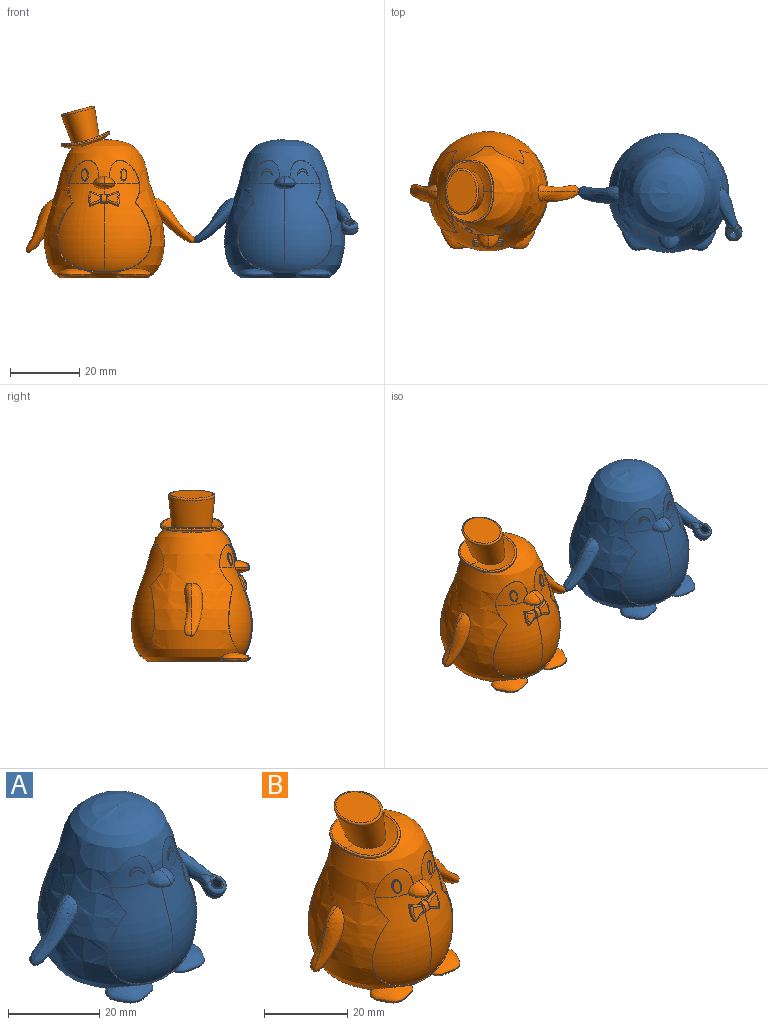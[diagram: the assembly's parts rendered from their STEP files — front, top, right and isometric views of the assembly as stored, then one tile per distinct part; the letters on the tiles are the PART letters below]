
ASSEMBLY  parts=2 mates=1
PART A: 47 faces, bbox 47.7x34.8x41.4 mm
  f0: bspline ~14.59x10.37mm, area 63.4mm2, adj f1,f6,f37,f38,f39,f40,f41
  f1: bspline ~16.09x8.88mm, area 34.3mm2, adj f0,f6,f42
  f2: extruded ~3.22x1.83mm, area 1.6mm2, adj f4,f9,f43,f44
  f3: extruded ~3.04x1.72mm, area 1.2mm2, adj f4,f9,f43,f44
  f4: revolved ~3.35x1.88mm, area 2.4mm2, adj f2,f3,f43,f44
  f5: bspline ~0.66x0.4mm, area 0mm2, adj f6,f15,f28
  f6: revolved ~40x34.78mm, area -613.6mm2, adj f0,f1,f5,f10,f11,f12,f13,f14
  f7: revolved ~25.41x13.46mm, area 325.8mm2, adj f8,f14,f15,f17,f29
  f8: revolved ~25.41x13.46mm, area 325.8mm2, adj f7,f9,f12,f13,f30
  f9: revolved ~8.83x6.78mm, area 49.1mm2, adj f2,f3,f8,f12,f27,f43,f44
  f10: revolved ~32.45x27.32mm, area 791.3mm2, adj f6
  f11: plane 27.91x25mm, normal (0,0,-1), area 565.7mm2, adj f6,f22,f24
  f12: bspline ~12.26x8.93mm, area 5.9mm2, adj f6,f8,f9,f13,f16,f27
  f13: bspline ~20.28x13.66mm, area 7.8mm2, adj f6,f8,f12,f14
  f14: bspline ~20.28x13.66mm, area 7.8mm2, adj f6,f7,f13,f15
  f15: bspline ~12.25x8.92mm, area 5.9mm2, adj f5,f6,f7,f14,f17,f28
  f16: bspline ~0.66x0.4mm, area 0mm2, adj f6,f12,f27
  f17: revolved ~8.83x6.78mm, area 49mm2, adj f7,f15,f18,f19,f28,f45,f46
  f18: extruded ~3.22x1.83mm, area 1.6mm2, adj f17,f20,f45,f46
  f19: extruded ~3.04x1.72mm, area 1.2mm2, adj f17,f20,f45,f46
  f20: revolved ~3.35x1.88mm, area 2.4mm2, adj f18,f19,f45,f46
  f21: bspline ~10.19x8.58mm, area 33.1mm2, adj f6,f22
  f22: bspline ~10.19x8.58mm, area 20.6mm2, adj f6,f11,f21
  f23: bspline ~10.19x8.58mm, area 33.1mm2, adj f6,f24
  f24: bspline ~10.19x8.58mm, area 20.6mm2, adj f6,f11,f23
  f25: bspline ~13.75x13.07mm, area 24.4mm2, adj f6,f26
  f26: bspline ~12.41x11.83mm, area 16mm2, adj f6,f25
  f27: bspline ~4.05x3.2mm, area 14.3mm2, adj f6,f9,f12,f16,f28,f30
  f28: bspline ~4.05x3.2mm, area 14.3mm2, adj f5,f6,f15,f17,f27,f29
  f29: bspline ~3.87x3.19mm, area 6.5mm2, adj f7,f28,f30
  f30: bspline ~3.87x3.19mm, area 6.5mm2, adj f8,f27,f29
  f31: cylinder r=2.43mm len=4.86mm, axis (0,0.5,-0.87), area 10.4mm2, adj f35,f36,f40,f41
  f32: plane 2.9x2.34mm, normal (0,-0.5,0.87), area 1.9mm2, adj f34,f36,f37
  f33: plane 2.87x2.48mm, normal (0,0.5,-0.87), area 2.3mm2, adj f34,f35
  f34: cylinder r=1.15mm len=3.75mm, axis (0,-0.5,0.87), area 21.7mm2, adj f32,f33,f37
  f35: bspline ~4.86x4.39mm, area 16.4mm2, adj f31,f33,f42
  f36: bspline ~4.85x4.09mm, area 15.5mm2, adj f31,f32,f38,f39
  f37: bspline ~1.5x0.98mm, area 1mm2, adj f0,f32,f34,f38,f39
  f38: bspline ~2.14x1.54mm, area 2.6mm2, adj f0,f36,f37,f40
  f39: bspline ~2.69x2.17mm, area 5.3mm2, adj f0,f36,f37,f41
  f40: bspline ~1.14x1.01mm, area 0.9mm2, adj f0,f31,f38,f42
  f41: bspline ~2.7x1.87mm, area 2.2mm2, adj f0,f31,f39,f42
  f42: bspline ~4.24x2.32mm, area 5.8mm2, adj f1,f35,f40,f41
  f43: cylinder r=0.05mm len=0.37mm, axis (0,1,0), area 0mm2, adj f2,f3,f4,f9
  f44: cylinder r=0.05mm len=0.32mm, axis (0,1,0), area 0mm2, adj f2,f3,f4,f9
  f45: cylinder r=0.05mm len=0.32mm, axis (0,1,0), area 0mm2, adj f17,f18,f19,f20
  f46: cylinder r=0.05mm len=0.37mm, axis (0,1,0), area 0mm2, adj f17,f18,f19,f20
PART B: 75 faces, bbox 50.8x36.4x52.7 mm
  f0: bspline ~0.66x0.4mm, area 0mm2, adj f1,f52,f53
  f1: bspline ~12.26x8.93mm, area 5.9mm2, adj f0,f2,f6,f51,f52,f53
  f2: revolved ~8.83x6.78mm, area 45.1mm2, adj f1,f3,f5,f6,f52
  f3: bspline ~3.49x2mm, area 2.9mm2, adj f2,f4,f5
  f4: revolved ~3.11x1.97mm, area 4.5mm2, adj f3
  f5: extruded ~3.5x1.98mm, area 2.3mm2, adj f2,f3
  f6: revolved ~25.41x13.46mm, area 323.8mm2, adj f1,f2,f7,f17,f30,f31,f32,f33
  f7: bspline ~3.87x3.19mm, area 6.5mm2, adj f6,f8,f52
  f8: bspline ~3.87x3.19mm, area 6.5mm2, adj f7,f9,f50
  f9: bspline ~4.05x3.2mm, area 14.3mm2, adj f8,f10,f14,f16,f52,f53
  f10: revolved ~8.83x6.78mm, area 45mm2, adj f9,f11,f13,f14,f50
  f11: bspline ~3.49x2mm, area 2.9mm2, adj f10,f12,f13
  f12: revolved ~3.11x1.97mm, area 4.5mm2, adj f11
  f13: extruded ~3.5x1.98mm, area 2.3mm2, adj f10,f11
  f14: bspline ~12.25x8.92mm, area 5.9mm2, adj f9,f10,f15,f16,f50,f53
  f15: bspline ~20.28x13.66mm, area 7.8mm2, adj f14,f50,f51,f53
  f16: bspline ~0.66x0.4mm, area 0mm2, adj f9,f14,f53
  f17: plane 0.95x0.69mm, normal (1,0,0), area 0.1mm2, adj f6,f18,f29,f32
  f18: plane 2.97x1.31mm, normal (-0.38,-0.32,-0.87), area 1.6mm2, adj f17,f19,f29,f30
  f19: bspline ~0.49x0.24mm, area 0.1mm2, adj f18,f20,f28,f30
  f20: cylinder r=6mm len=4.22mm, axis (0,0.94,-0.34), area 2.2mm2, adj f19,f21,f27,f30
  f21: bspline ~0.49x0.24mm, area 0.1mm2, adj f20,f22,f26,f30
  f22: plane 2.97x1.31mm, normal (-0.38,0.32,0.87), area 1.6mm2, adj f21,f23,f30,f31
  f23: bspline ~3.77x1.71mm, area 2.5mm2, adj f22,f24,f26,f32
  f24: plane 3x2.99mm, normal (0,-0.94,0.34), area 6.2mm2, adj f23,f25,f27,f29
  f25: plane 1.42x0.5mm, normal (1,0,0), area 0.1mm2, adj f24,f29,f32
  f26: bspline ~0.69x0.5mm, area 0.1mm2, adj f21,f23,f27
  f27: bspline ~4.14x1.89mm, area 3.1mm2, adj f20,f24,f26,f28
  f28: bspline ~0.77x0.36mm, area 0.1mm2, adj f19,f27,f29
  f29: bspline ~3.77x1.98mm, area 2.5mm2, adj f17,f18,f24,f25,f28
  f30: plane 4.21x3.51mm, normal (0,0.94,-0.34), area 11.3mm2, adj f6,f18,f19,f20,f21,f22
  f31: plane 0.54x0.21mm, normal (1,0,0), area 0mm2, adj f6,f22,f32
  f32: bspline ~2.79x2.15mm, area 2mm2, adj f6,f17,f23,f25,f31,f33
  f33: extruded ~2.71x1.93mm, area 6.3mm2, adj f6,f32,f34,f50
  f34: bspline ~2.79x2.15mm, area 2mm2, adj f33,f35,f47,f48,f49,f50
  f35: plane 0.95x0.69mm, normal (-1,0,0), area 0.1mm2, adj f34,f36,f46,f50
  f36: plane 2.97x1.31mm, normal (0.38,-0.32,-0.87), area 1.6mm2, adj f35,f37,f45,f46
  f37: plane 4.21x3.51mm, normal (0,0.94,-0.34), area 11.3mm2, adj f36,f38,f39,f44,f45,f50
  f38: plane 2.97x1.31mm, normal (0.38,0.32,0.87), area 1.6mm2, adj f37,f39,f48,f49
  f39: bspline ~0.54x0.26mm, area 0.1mm2, adj f37,f38,f40,f44
  f40: bspline ~0.69x0.5mm, area 0.1mm2, adj f39,f41,f48
  f41: bspline ~4.14x1.89mm, area 3.1mm2, adj f40,f42,f43,f44
  f42: plane 3x2.99mm, normal (0,-0.94,0.34), area 6.2mm2, adj f41,f46,f47,f48
  f43: bspline ~0.77x0.36mm, area 0.1mm2, adj f41,f45,f46
  f44: cylinder r=6mm len=4.22mm, axis (0,0.94,-0.34), area 2.2mm2, adj f37,f39,f41,f45
  f45: bspline ~0.54x0.26mm, area 0.1mm2, adj f36,f37,f43,f44
  f46: bspline ~3.77x1.98mm, area 2.5mm2, adj f35,f36,f42,f43,f47
  f47: plane 1.42x0.5mm, normal (-1,0,0), area 0.1mm2, adj f34,f42,f46
  f48: bspline ~3.77x1.71mm, area 2.5mm2, adj f34,f38,f40,f42
  f49: plane 0.54x0.21mm, normal (-1,0,0), area 0mm2, adj f34,f38,f50
  f50: revolved ~25.41x13.46mm, area 323.8mm2, adj f6,f8,f10,f14,f15,f33,f34,f35
  f51: bspline ~20.28x13.66mm, area 7.8mm2, adj f1,f6,f15,f53
  f52: bspline ~4.05x3.2mm, area 14.3mm2, adj f0,f1,f2,f7,f9,f53
  f53: revolved ~40x34.78mm, area 860.4mm2, adj f0,f1,f9,f14,f15,f16,f51,f52
  f54: revolved ~32.45x27.32mm, area 791.3mm2, adj f53
  f55: bspline ~16.14x9.95mm, area 82.2mm2, adj f53,f56
  f56: bspline ~16.03x9.81mm, area 57.5mm2, adj f53,f55
  f57: offset ~15.12x12.76mm, area 62.8mm2, adj f53,f58,f67
  f58: bspline ~14.15x10.15mm, area 17.3mm2, adj f57,f59,f66
  f59: bspline ~13.97x10.41mm, area 16.5mm2, adj f58,f60,f65
  f60: bspline ~13.52x11.16mm, area 61.9mm2, adj f59,f61,f64
  f61: bspline ~13.38x10.99mm, area 305.1mm2, adj f60,f62,f64
  f62: bspline ~13.56x9.79mm, area 31.4mm2, adj f61,f63
  f63: plane 12.47x8.66mm, normal (-0.26,0,0.97), area 86.1mm2, adj f62
  f64: bspline ~13.52x11.16mm, area 61.9mm2, adj f60,f61,f65
  f65: bspline ~13.97x10.41mm, area 16.5mm2, adj f59,f64,f66
  f66: bspline ~14.15x10.15mm, area 17.3mm2, adj f58,f65,f67
  f67: offset ~15.12x12.76mm, area 63.2mm2, adj f53,f57,f66
  f68: bspline ~10.19x8.58mm, area 33.1mm2, adj f53,f74
  f69: bspline ~10.19x8.58mm, area 33.1mm2, adj f53,f70
  f70: bspline ~10.19x8.58mm, area 20.6mm2, adj f53,f69,f73
  f71: bspline ~12.41x11.83mm, area 32.3mm2, adj f53,f72
  f72: bspline ~13.75x13.07mm, area 24.4mm2, adj f53,f71
  f73: plane 27.91x25mm, normal (0,0,-1), area 565.7mm2, adj f53,f70,f74
  f74: bspline ~10.19x8.58mm, area 20.6mm2, adj f53,f68,f73
PLACE A t=(-16.63,-12.53,-9.91)mm
PLACE B t=(-68.92,-12.11,-9.91)mm
MATE planar A.f11 <-> B.f73  axis (0,0,-1) through (-16.63,-14.14,-9.91)mm
